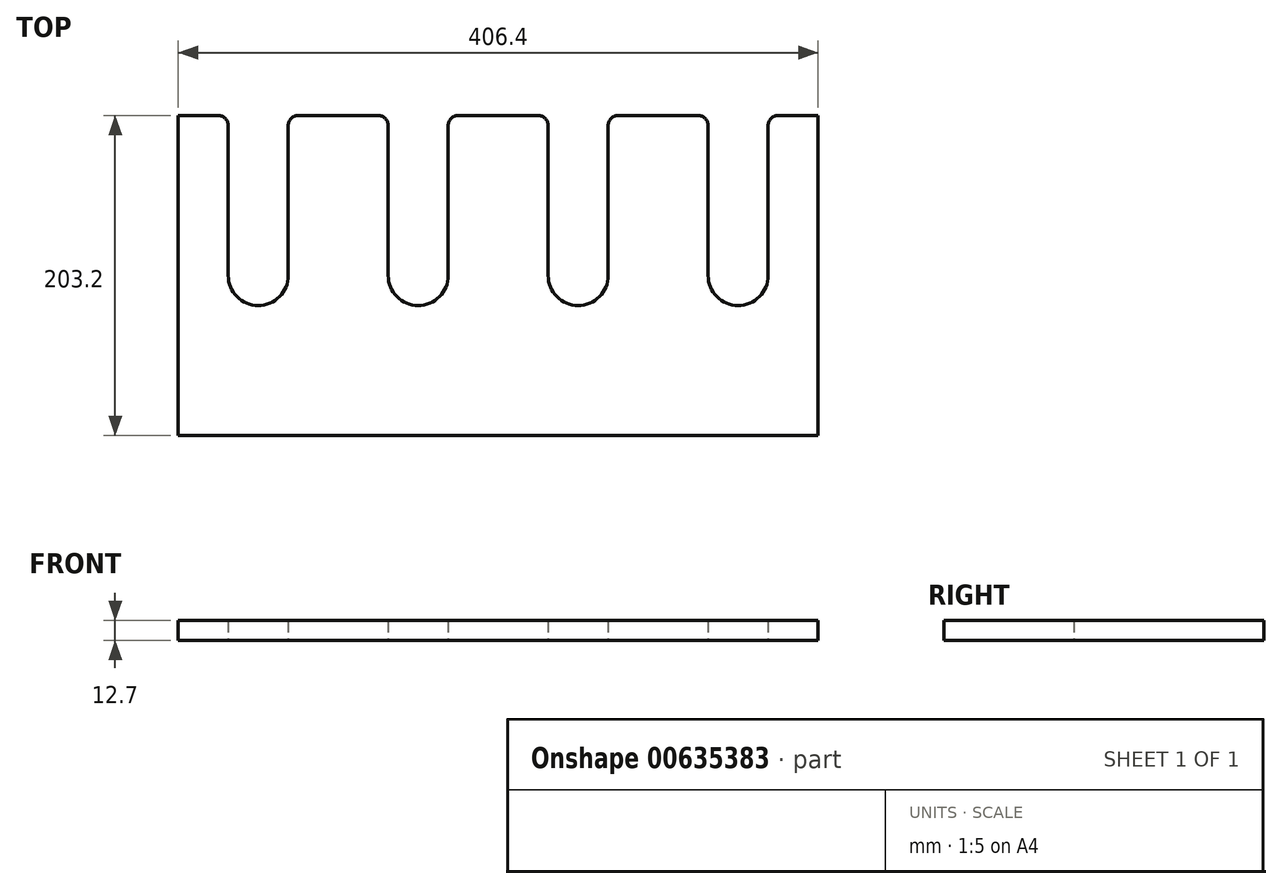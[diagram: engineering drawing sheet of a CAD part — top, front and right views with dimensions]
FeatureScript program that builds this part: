
annotation { "Feature Type Name" : "Feature", "Feature Type Description" : "" }
export const myFeature = defineFeature(function(context is Context, id is Id, definition is map)
    precondition{}
    {
        {
            var Q0;
            Q0=qCreatedBy(makeId("Top.planeOp"),FACE);
            var sketch = newSketch(context, id + "F0", { "sketchPlane" : qUnion([Q0])});
            skLineSegment(sketch, "E0.bottom", {"start": v(0, 0) * mm, "end": v(406.4, 0) * mm});
            skLineSegment(sketch, "E0.top", {"start": v(0, 203.2) * mm, "end": v(25.4, 203.2) * mm});
            skLineSegment(sketch, "E0.left", {"start": v(0, 0) * mm, "end": v(0, 203.2) * mm});
            skLineSegment(sketch, "E0.right", {"start": v(406.4, 0) * mm, "end": v(406.4, 203.2) * mm});
            skLineSegment(sketch, "E1.top", {"start": v(50.8, 82.55) * mm, "end": v(50.8, 82.55) * mm});
            skLineSegment(sketch, "E1.left", {"start": v(31.75, 196.85) * mm, "end": v(31.75, 101.6) * mm});
            skLineSegment(sketch, "E1.right", {"start": v(69.85, 196.85) * mm, "end": v(69.85, 101.6) * mm});
            skLineSegment(sketch, "E2.top", {"start": v(152.4, 82.55) * mm, "end": v(152.4, 82.55) * mm});
            skLineSegment(sketch, "E2.left", {"start": v(133.35, 196.85) * mm, "end": v(133.35, 101.6) * mm});
            skLineSegment(sketch, "E2.right", {"start": v(171.45, 196.85) * mm, "end": v(171.45, 101.6) * mm});
            skLineSegment(sketch, "E3.top", {"start": v(254, 82.55) * mm, "end": v(254, 82.55) * mm});
            skLineSegment(sketch, "E3.left", {"start": v(234.95, 196.85) * mm, "end": v(234.95, 101.6) * mm});
            skLineSegment(sketch, "E3.right", {"start": v(273.05, 196.85) * mm, "end": v(273.05, 101.6) * mm});
            skLineSegment(sketch, "E4.top", {"start": v(355.6, 82.55) * mm, "end": v(355.6, 82.55) * mm});
            skLineSegment(sketch, "E4.left", {"start": v(336.55, 196.85) * mm, "end": v(336.55, 101.6) * mm});
            skLineSegment(sketch, "E4.right", {"start": v(374.65, 196.85) * mm, "end": v(374.65, 101.6) * mm});
            skLineSegment(sketch, "E5.trimOffspring", {"start": v(76.2, 203.2) * mm, "end": v(127, 203.2) * mm});
            skLineSegment(sketch, "E6.trimOffspring", {"start": v(177.8, 203.2) * mm, "end": v(228.6, 203.2) * mm});
            skLineSegment(sketch, "E7.trimOffspring", {"start": v(279.4, 203.2) * mm, "end": v(330.2, 203.2) * mm});
            skLineSegment(sketch, "E8.trimOffspring", {"start": v(381, 203.2) * mm, "end": v(406.4, 203.2) * mm});
            skPoint(sketch, "E9.visualSharp", {"position": v(31.75, 82.55) * mm});
            skArc(sketch, "E9.filletArc", {"start": v(31.75, 101.6) * mm, "mid": v(37.33, 88.13) * mm, "end": v(50.8, 82.55) * mm});
            skPoint(sketch, "E10.visualSharp", {"position": v(69.85, 82.55) * mm});
            skArc(sketch, "E10.filletArc", {"start": v(50.8, 82.55) * mm, "mid": v(64.27, 88.13) * mm, "end": v(69.85, 101.6) * mm});
            skPoint(sketch, "E11.visualSharp", {"position": v(133.35, 82.55) * mm});
            skArc(sketch, "E11.filletArc", {"start": v(133.35, 101.6) * mm, "mid": v(138.93, 88.13) * mm, "end": v(152.4, 82.55) * mm});
            skPoint(sketch, "E12.visualSharp", {"position": v(171.45, 82.55) * mm});
            skArc(sketch, "E12.filletArc", {"start": v(152.4, 82.55) * mm, "mid": v(165.87, 88.13) * mm, "end": v(171.45, 101.6) * mm});
            skPoint(sketch, "E13.visualSharp", {"position": v(234.95, 82.55) * mm});
            skArc(sketch, "E13.filletArc", {"start": v(234.95, 101.6) * mm, "mid": v(240.53, 88.13) * mm, "end": v(254, 82.55) * mm});
            skPoint(sketch, "E14.visualSharp", {"position": v(273.05, 82.55) * mm});
            skArc(sketch, "E14.filletArc", {"start": v(254, 82.55) * mm, "mid": v(267.47, 88.13) * mm, "end": v(273.05, 101.6) * mm});
            skPoint(sketch, "E15.visualSharp", {"position": v(336.55, 82.55) * mm});
            skArc(sketch, "E15.filletArc", {"start": v(336.55, 101.6) * mm, "mid": v(342.13, 88.13) * mm, "end": v(355.6, 82.55) * mm});
            skPoint(sketch, "E16.visualSharp", {"position": v(374.65, 82.55) * mm});
            skArc(sketch, "E16.filletArc", {"start": v(355.6, 82.55) * mm, "mid": v(369.07, 88.13) * mm, "end": v(374.65, 101.6) * mm});
            skPoint(sketch, "E17.visualSharp", {"position": v(31.75, 203.2) * mm});
            skArc(sketch, "E17.filletArc", {"start": v(31.75, 196.85) * mm, "mid": v(29.9, 201.34) * mm, "end": v(25.4, 203.2) * mm});
            skPoint(sketch, "E18.visualSharp", {"position": v(69.85, 203.2) * mm});
            skArc(sketch, "E18.filletArc", {"start": v(76.2, 203.2) * mm, "mid": v(71.7, 201.34) * mm, "end": v(69.85, 196.85) * mm});
            skPoint(sketch, "E19.visualSharp", {"position": v(133.35, 203.2) * mm});
            skArc(sketch, "E19.filletArc", {"start": v(133.35, 196.85) * mm, "mid": v(131.5, 201.34) * mm, "end": v(127, 203.2) * mm});
            skPoint(sketch, "E20.visualSharp", {"position": v(171.45, 203.2) * mm});
            skArc(sketch, "E20.filletArc", {"start": v(177.8, 203.2) * mm, "mid": v(173.3, 201.34) * mm, "end": v(171.45, 196.85) * mm});
            skPoint(sketch, "E21.visualSharp", {"position": v(234.95, 203.2) * mm});
            skArc(sketch, "E21.filletArc", {"start": v(234.95, 196.85) * mm, "mid": v(233.1, 201.34) * mm, "end": v(228.6, 203.2) * mm});
            skPoint(sketch, "E22.visualSharp", {"position": v(273.05, 203.2) * mm});
            skArc(sketch, "E22.filletArc", {"start": v(279.4, 203.2) * mm, "mid": v(274.9, 201.34) * mm, "end": v(273.05, 196.85) * mm});
            skPoint(sketch, "E23.visualSharp", {"position": v(374.65, 203.2) * mm});
            skArc(sketch, "E23.filletArc", {"start": v(381, 203.2) * mm, "mid": v(376.5, 201.34) * mm, "end": v(374.65, 196.85) * mm});
            skPoint(sketch, "E24.visualSharp", {"position": v(336.55, 203.2) * mm});
            skArc(sketch, "E24.filletArc", {"start": v(336.55, 196.85) * mm, "mid": v(334.7, 201.34) * mm, "end": v(330.2, 203.2) * mm});
            skSolve(sketch);
        }
        {
            var Q0;
            Q0=makeQuery(id+"F0.imprint","IMPRINT",FACE,{"disambiguationData":[TD([[makeQuery(id+"F0.imprint","IMPRINT",EDGE,{"derivedFrom":sQuery(id+"F0.wireOp",EDGE,"E0.bottom")}),1.0]])]});
            extrude(context, id + "F1", {"entities" : qUnion([Q0]), "depth" : 12.7 * mm, "offsetDistance" : 25.4 * mm});
        }
    });
